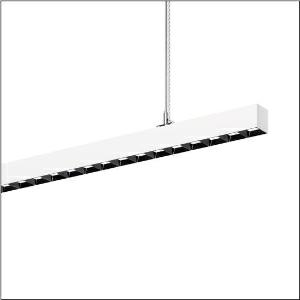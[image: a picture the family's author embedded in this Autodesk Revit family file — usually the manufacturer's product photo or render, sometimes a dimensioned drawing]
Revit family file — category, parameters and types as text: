
# Revit family: silica_r__21_51mx32tat7w_976d
name_source: partatom
category: Lighting Fixtures
units: mm (PartAtom-declared; Revit-internal decimal feet)

## family parameters
Cut with Voids When Loaded = No
Host = Face
Light Source = No
Part Type = Normal
Room Calculation Point = No
Round Connector Dimension = Use Diameter
Shared = No

## types (1)
- --- (1 x LED, 6220 lm, 53.4 W, 6500K)
    Apparent Load = 53 VA
    CIE Flux Codes = 84 99 100 60 100
    Color Rendering = 80
    Color Temperature = 6500K
    Default Elevation = 1800 mm
    Description = Silica® 21, office luminaire, primary light control with darklight reflector, of PMMA, black, CAT 2 (L<= 3000cd/m²), light emission: direct/indirect distribution, primary light characteristic: symmetric, installation type: suspended mounting, LED, rated luminous flux: 6.220lm, luminous efficacy: 111lm/W, light colour: 8tw, colour temperature: 2700..6500K, control gear: ECG DALI, with terminal, 3+2-pole, max. 2.5mm², mains connection: 220..240V, AC, 50/60Hz, rated input power: 56.1W, luminaire housing, of aluminium, traffic white (RAL 9016), length: 1.204mm, width: 53mm, height: 53mm, protection rating (complete): IP20, insulation class (complete): insulation class I (protective earthing), certification: CE, permissible operating ambient temperature: 0..+35°C, standard: EN 50419, packaging unit: 1 piece
    Height = 53 mm
    Lamp = 1 x LED
    Lamp Light Flux = 6220 lm
    Lamp Power = 53.4 W
    Lamp count = 1
    Length = 1204 mm
    Luminous efficacy = 116 lm/W
    Manufacturer = Siteco
    ModVariant = No
    Model = 51MX32TAT7W
    Mounting Place = Ceiling
    Mounting Type = Pendant
    Number of Poles = 1
    OnlyDefault = Yes
    Power Factor = 1
    Product Name = Silica® 21
    Product group = office luminaire | ceiling pendant
    ProductGroupID = 902
    Protection Class = Protection class I
    Protection Degree = IP 20
    RLX_Detail_Level = 1
    RLX_Emergency_Light_Flux = 0 lm
    RLX_Emergency_Type = 0
    RLX_Emergency_Type_DB = No
    RlxData = <blob elided: 40497 chars, md5=04a9781c>
    Socket = socket
    Standby Power = 0 W
    System Light Flux = 6220 lm
    System Power = 53 W
    Type Comments = individual setting
    Type Image = l_1335871.jpg
    URL = http://relux.com
    VarID = @adj_109765
    Voltage = 0 V
    Weight = 0.00 kg
    Width = 53 mm

## geometry (parser evidence)
native form markers: Blend x4, Sweep x14
no freeform markers — native parametric forms only
